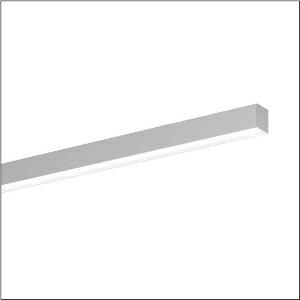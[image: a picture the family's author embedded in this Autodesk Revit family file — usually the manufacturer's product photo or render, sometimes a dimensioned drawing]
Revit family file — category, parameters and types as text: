
# Revit family: silica_r__21_51mx23tat4s_c658
name_source: partatom
category: Lighting Fixtures
units: mm (PartAtom-declared; Revit-internal decimal feet)

## family parameters
Cut with Voids When Loaded = No
Host = Face
Light Source = No
Part Type = Normal
Room Calculation Point = No
Round Connector Dimension = Use Diameter
Shared = No

## types (1)
- --- (1 x LED, 3230 lm, 32.4 W, 6500K)
    Apparent Load = 32 VA
    CIE Flux Codes = 78 96 99 100 100
    Color Rendering = 80
    Color Temperature = 6500K
    Default Elevation = 1800 mm
    Description = Silica® 21, office luminaire, primary optical cover: prismatic diffuser, of PMMA, CAT 2 (L<= 3000cd/m²), light emission: direct distribution, primary light characteristic: symmetric, installation type: surface-mounted, LED, rated luminous flux: 3.230lm, luminous efficacy: 95lm/W, light colour: 8tw, colour temperature: 2700..6500K, control gear: ECG DALI, with terminal, 3+2-pole, max. 2.5mm², mains connection: 220..240V, AC, 50/60Hz, rated input power: 34W, luminaire housing, of aluminium, metallic grey (RAL 9006), length: 1.204mm, width: 53mm, height: 53mm, protection rating (complete): IP20, insulation class (complete): insulation class I (protective earthing), certification: CE, permissible operating ambient temperature: 0..+35°C, standard: EN 50419, packaging unit: 1 piece
    Height = 0 mm  [stored 0 ft]
    Lamp = 1 x LED
    Lamp Light Flux = 3230 lm
    Lamp Power = 32.4 W
    Lamp count = 1
    Length = 1204 mm
    Luminous efficacy = 100 lm/W
    Manufacturer = Siteco
    ModVariant = No
    Model = 51MX23TAT4S
    Mounting Place = Ceiling
    Mounting Type = Recessed
    Number of Poles = 1
    OnlyDefault = Yes
    Power Factor = 1
    Product Name = Silica® 21
    Product group = office luminaire | ceiling recessed
    ProductGroupID = 401
    Protection Class = Protection class I
    Protection Degree = IP 20
    RLX_Detail_Level = 1
    RLX_Emergency_Light_Flux = 0 lm
    RLX_Emergency_Type = 0
    RLX_Emergency_Type_DB = No
    RlxData = <blob elided: 18041 chars, md5=c11317de>
    Socket = socket
    Standby Power = 0 W
    System Light Flux = 3230 lm
    System Power = 32 W
    Type Comments = individual setting
    Type Image = l_1297768.jpg
    URL = http://relux.com
    VarID = @adj_071125
    Voltage = 0 V
    Weight = 0.00 kg
    Width = 53 mm

note: [stored X ft] marks values corroborated as IEEE doubles in the binary element streams (Revit-internal decimal feet)

## geometry (parser evidence)
native form markers: Blend x4, Sweep x10
no freeform markers — native parametric forms only
